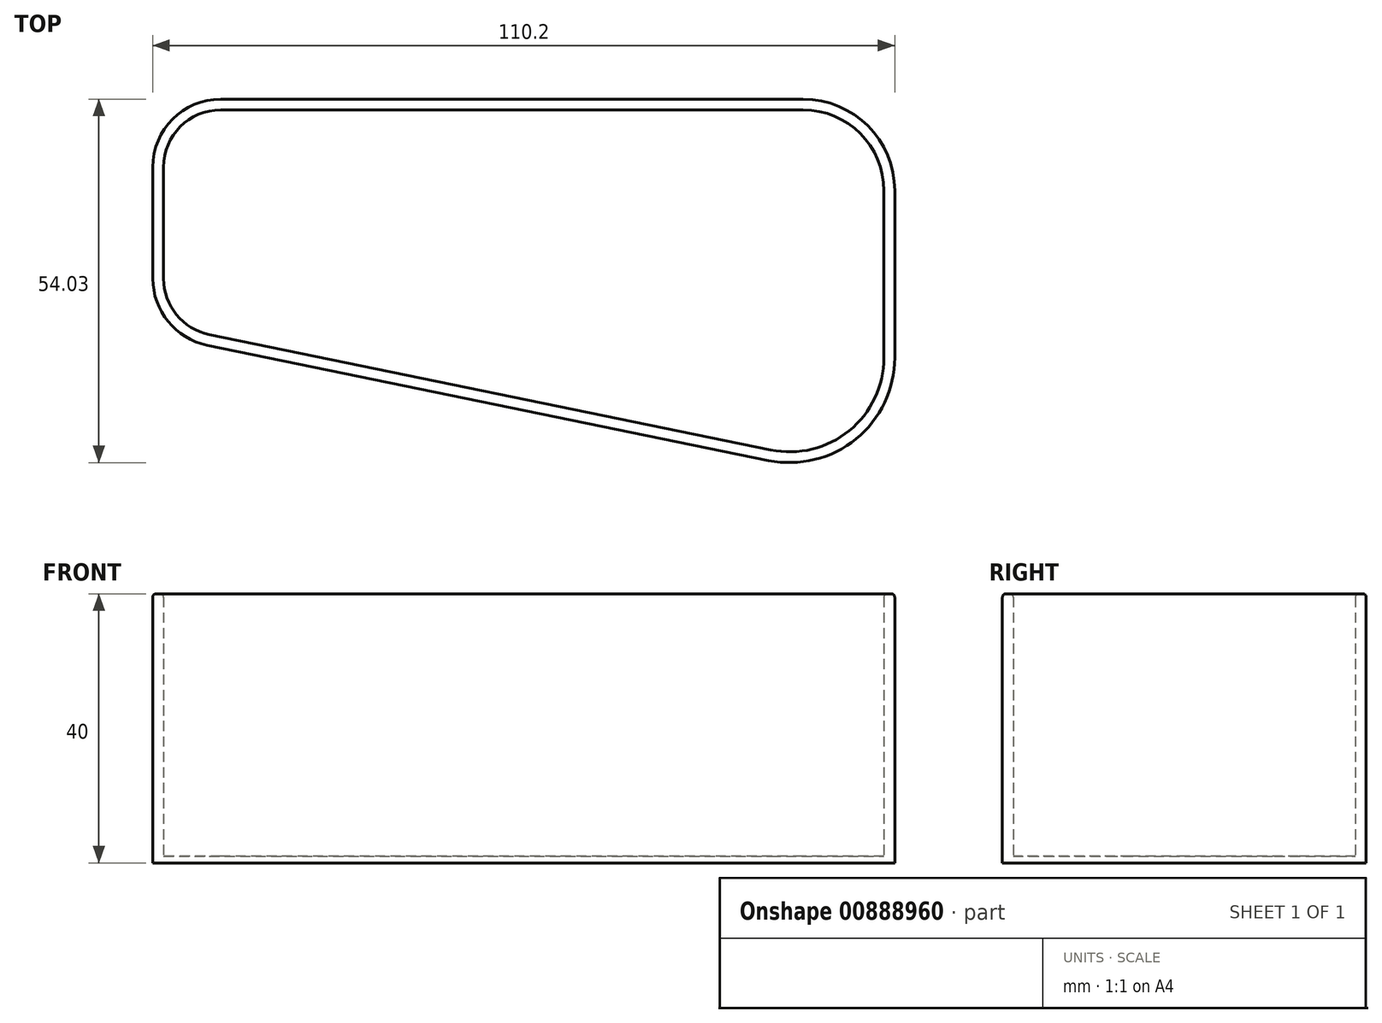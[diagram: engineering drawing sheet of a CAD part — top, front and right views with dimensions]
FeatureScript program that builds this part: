
annotation { "Feature Type Name" : "Feature", "Feature Type Description" : "" }
export const myFeature = defineFeature(function(context is Context, id is Id, definition is map)
    precondition{}
    {
        {
            var Q0;
            Q0=qCreatedBy(makeId("Top.planeOp"),FACE);
            var sketch = newSketch(context, id + "F0", { "sketchPlane" : qUnion([Q0])});
            skLineSegment(sketch, "E0", {"start": v(-12, 0) * mm, "end": v(-98.5, 0) * mm});
            skLineSegment(sketch, "E1", {"start": v(-107, -8.5) * mm, "end": v(-107, -25.07) * mm});
            skLineSegment(sketch, "E2", {"start": v(-100.21, -33.4) * mm, "end": v(-16.82, -50.54) * mm});
            skLineSegment(sketch, "E3", {"start": v(0, -36.83) * mm, "end": v(0, -12) * mm});
            skPoint(sketch, "E4.visualSharp", {"position": v(-107, 0) * mm});
            skArc(sketch, "E4.filletArc", {"start": v(-98.5, 0) * mm, "mid": v(-104.51, -2.49) * mm, "end": v(-107, -8.5) * mm});
            skPoint(sketch, "E5.visualSharp", {"position": v(-107, -32) * mm});
            skArc(sketch, "E5.filletArc", {"start": v(-107, -25.07) * mm, "mid": v(-105.09, -30.44) * mm, "end": v(-100.21, -33.4) * mm});
            skPoint(sketch, "E6.visualSharp", {"position": v(0, 0) * mm});
            skArc(sketch, "E6.filletArc", {"start": v(0, -12) * mm, "mid": v(-3.51, -3.51) * mm, "end": v(-12, 0) * mm});
            skPoint(sketch, "E7.visualSharp", {"position": v(0, -54) * mm});
            skArc(sketch, "E7.filletArc", {"start": v(-16.82, -50.54) * mm, "mid": v(-5.15, -47.68) * mm, "end": v(0, -36.83) * mm});
            skArc(sketch, "E8.0", {"start": v(1.6, -12) * mm, "mid": v(-2.38, -2.38) * mm, "end": v(-12, 1.6) * mm});
            skLineSegment(sketch, "E8.1", {"start": v(1.6, -36.83) * mm, "end": v(1.6, -12) * mm});
            skLineSegment(sketch, "E8.2", {"start": v(-12, 1.6) * mm, "end": v(-98.5, 1.6) * mm});
            skArc(sketch, "E8.3", {"start": v(-17.14, -52.1) * mm, "mid": v(-4.14, -48.92) * mm, "end": v(1.6, -36.83) * mm});
            skArc(sketch, "E8.4", {"start": v(-98.5, 1.6) * mm, "mid": v(-105.64, -1.36) * mm, "end": v(-108.6, -8.5) * mm});
            skLineSegment(sketch, "E8.5", {"start": v(-108.6, -8.5) * mm, "end": v(-108.6, -25.07) * mm});
            skArc(sketch, "E8.6", {"start": v(-108.6, -25.07) * mm, "mid": v(-106.33, -31.45) * mm, "end": v(-100.53, -34.96) * mm});
            skLineSegment(sketch, "E8.7", {"start": v(-100.53, -34.96) * mm, "end": v(-17.14, -52.1) * mm});
            skSolve(sketch);
        }
        {
            var Q0;
            Q0=makeQuery(id+"F0.imprint","IMPRINT",FACE,{"disambiguationData":[TD([[makeQuery(id+"F0.imprint","IMPRINT",EDGE,{"derivedFrom":sQuery(id+"F0.wireOp",EDGE,"E0")}),1.0]])]});
            extrude(context, id + "F1", {"entities" : qUnion([Q0]), "depth" : 1 * mm, "offsetDistance" : 25 * mm});
        }
        {
            var Q0;
            Q0 = qSketchRegion(id + "F0", true);
            extrude(context, id + "F2", {"entities" : qUnion([Q0]), "operationType" : NewBodyOperationType.ADD, "depth" : 40 * mm, "offsetDistance" : 25 * mm});
        }
        {
            var Q0;
            Q0=makeQuery(id+"F2.opExtrude","CAP_EDGE",EDGE,{"disambiguationData":[OSD([sQuery(id+"F0.wireOp",EDGE,"E8.7")])],"isStart":false});
            var Q1;
            Q1=makeQuery(id+"F2.opExtrude","CAP_EDGE",EDGE,{"disambiguationData":[OSD([sQuery(id+"F0.wireOp",EDGE,"E2")])],"isStart":false});
            fillet(context, id + "F3", {"entities" : qUnion([Q0, Q1]), "radius" : .5 * mm, "tangentPropagation" : true, "allowEdgeOverflow" : false});
        }
    });
